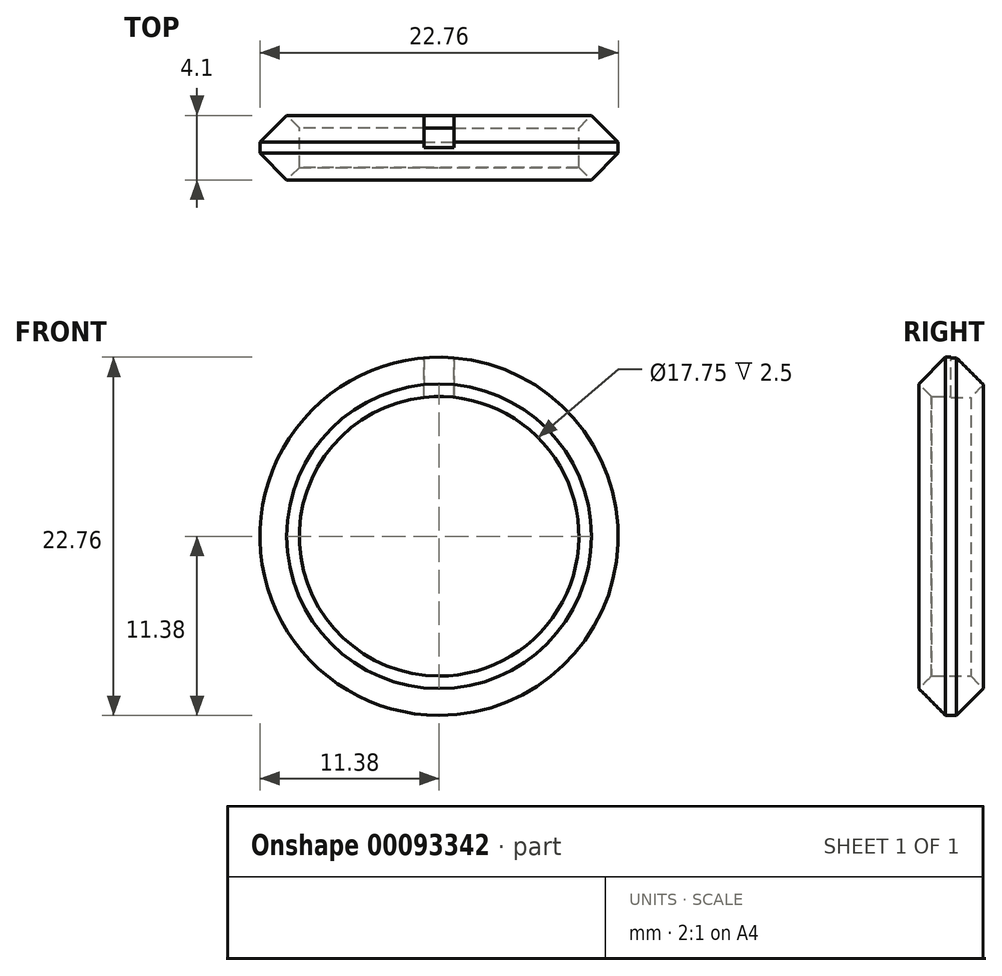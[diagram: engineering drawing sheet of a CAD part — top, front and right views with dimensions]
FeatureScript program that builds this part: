
annotation { "Feature Type Name" : "Feature", "Feature Type Description" : "" }
export const myFeature = defineFeature(function(context is Context, id is Id, definition is map)
    precondition{}
    {
        {
            var Q0;
            Q0=qCreatedBy(makeId("Front.planeOp"),FACE);
            var sketch = newSketch(context, id + "F0", { "sketchPlane" : qUnion([Q0])});
            skCircle(sketch, "E0", {"center": v(0, 0) * mm, "radius": 8.88 * mm});
            skCircle(sketch, "E1.0", {"center": v(0, 0) * mm, "radius": 11.38 * mm});
            skPoint(sketch, "E2", {"position": v(11.38, 0) * mm});
            skPoint(sketch, "E3", {"position": v(-11.38, 0) * mm});
            skLineSegment(sketch, "E4", {"start": v(11.38, 0) * mm, "end": v(11.38, 11.37) * mm});
            skLineSegment(sketch, "E5", {"start": v(11.38, 11.38) * mm, "end": v(0, 11.38) * mm});
            skLineSegment(sketch, "E6.MirrorCS", {"start": v(-11.38, 11.37) * mm, "end": v(0, 11.38) * mm});
            skLineSegment(sketch, "E7.MirrorCS", {"start": v(-11.38, 0) * mm, "end": v(-11.38, 11.37) * mm});
            skSolve(sketch);
        }
        {
            var Q0;
            Q0=makeQuery(id+"F0.imprint","IMPRINT",FACE,{"disambiguationData":[TD([[makeQuery(id+"F0.imprint","IMPRINT",EDGE,{"derivedFrom":sQuery(id+"F0.wireOp",EDGE,"E0")}),-1.0]])]});
            extrude(context, id + "F1", {"entities" : qUnion([Q0]), "depth" : 2.25 * mm, "hasSecondDirection" : true, "secondDirectionOppositeDirection" : true, "secondDirectionDepth" : 2.25 * mm});
        }
        {
            var Q0;
            Q0=makeQuery(id+"F1.opExtrude","CAP_EDGE",EDGE,{"disambiguationData":[OSD([sQuery(id+"F0.wireOp",EDGE,"E1.0")])],"isStart":false});
            var Q1;
            Q1=makeQuery(id+"F1.opExtrude","CAP_EDGE",EDGE,{"disambiguationData":[OSD([sQuery(id+"F0.wireOp",EDGE,"E1.0")])],"isStart":true});
            chamfer(context, id + "F2", {"entities" : qUnion([Q0, Q1]), "width" : 1.9 * mm, "tangentPropagation" : true});
        }
        {
            var Q0;
            Q0=qCreatedBy(makeId("Front.planeOp"),FACE);
            var sketch = newSketch(context, id + "F3", { "sketchPlane" : qUnion([Q0])});
            skLineSegment(sketch, "E8.bottom", {"start": v(0.95, 0) * mm, "end": v(-0.95, 0) * mm});
            skLineSegment(sketch, "E8.top", {"start": v(0.95, 23.78) * mm, "end": v(-0.95, 23.78) * mm});
            skLineSegment(sketch, "E8.left", {"start": v(0.95, 0) * mm, "end": v(0.95, 23.78) * mm});
            skLineSegment(sketch, "E8.right", {"start": v(-0.95, 0) * mm, "end": v(-0.95, 23.78) * mm});
            skPoint(sketch, "E8.middle", {"position": v(0, 11.9) * mm});
            skSolve(sketch);
        }
        {
            var Q0;
            Q0=makeQuery(id+"F3.imprint","IMPRINT",FACE,{"disambiguationData":[TD([[makeQuery(id+"F3.imprint","IMPRINT",EDGE,{"derivedFrom":sQuery(id+"F3.wireOp",EDGE,"E8.bottom")}),-1.0]])]});
            extrude(context, id + "F4", {"entities" : qUnion([Q0]), "operationType" : NewBodyOperationType.REMOVE, "oppositeDirection" : true, "depth" : 25 * mm});
        }
        {
            var Q0;
            Q0=makeQuery(id+"F1.opExtrude","CAP_EDGE",EDGE,{"disambiguationData":[OSD([sQuery(id+"F0.wireOp",EDGE,"E0")])],"isStart":true});
            var Q1;
            Q1=makeQuery(id+"F1.opExtrude","CAP_EDGE",EDGE,{"disambiguationData":[OSD([sQuery(id+"F0.wireOp",EDGE,"E0")])],"isStart":false});
            chamfer(context, id + "F5", {"entities" : qUnion([Q0, Q1]), "width" : 1 * mm, "tangentPropagation" : true});
        }
    });
